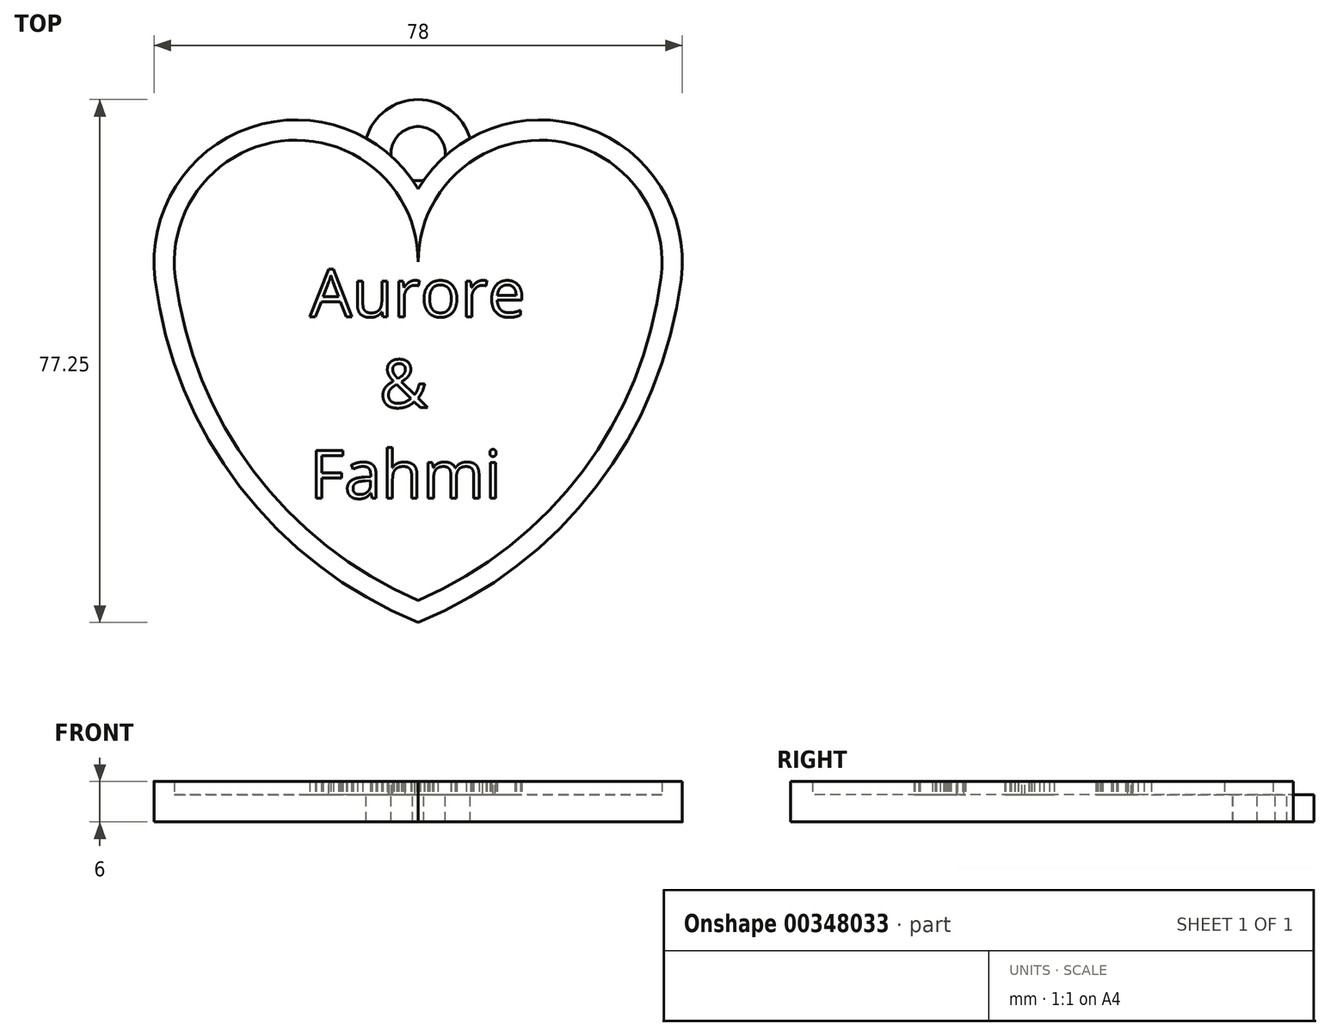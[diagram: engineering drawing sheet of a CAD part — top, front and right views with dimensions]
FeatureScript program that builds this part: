
annotation { "Feature Type Name" : "Feature", "Feature Type Description" : "" }
export const myFeature = defineFeature(function(context is Context, id is Id, definition is map)
    precondition{}
    {
        {
            var Q0;
            Q0=qCreatedBy(makeId("Top.planeOp"),FACE);
            var sketch = newSketch(context, id + "F0", { "sketchPlane" : qUnion([Q0])});
            skArc(sketch, "E0", {"start": v(35.87, -2.2) * mm, "mid": v(19.1, 17.97) * mm, "end": v(0, 0) * mm});
            skLineSegment(sketch, "E1", {"start": v(76.7, -35.15) * mm, "end": v(76.7, -35.15) * mm});
            skArc(sketch, "E2", {"start": v(0, 0) * mm, "mid": v(-19.1, 17.97) * mm, "end": v(-35.87, -2.2) * mm});
            skArc(sketch, "E3", {"start": v(0, -50) * mm, "mid": v(24.3, -30.88) * mm, "end": v(35.87, -2.2) * mm});
            skArc(sketch, "E4.MirrorCS", {"start": v(0, -50) * mm, "mid": v(-24.3, -30.88) * mm, "end": v(-35.87, -2.2) * mm});
            skArc(sketch, "E5", {"start": v(7.93, 14.92) * mm, "mid": v(0, 24) * mm, "end": v(-7.93, 14.92) * mm});
            skText(sketch, "E6", { "text": "Aurore\n    &\nFahmi", "fontName": "OpenSans-Regular.ttf"});
            skArc(sketch, "E7.0", {"start": v(0, -53.25) * mm, "mid": v(26.32, -33.2) * mm, "end": v(38.84, -2.56) * mm});
            skArc(sketch, "E7.1", {"start": v(0, -53.25) * mm, "mid": v(-26.32, -33.2) * mm, "end": v(-38.84, -2.56) * mm});
            skArc(sketch, "E7.2", {"start": v(0, 10.82) * mm, "mid": v(-24.84, 19.86) * mm, "end": v(-38.84, -2.56) * mm});
            skArc(sketch, "E7.3", {"start": v(38.84, -2.56) * mm, "mid": v(24.84, 19.86) * mm, "end": v(0, 10.82) * mm});
            skCircle(sketch, "E8", {"center": v(0, 16) * mm, "radius": 4 * mm});
            const initialGuessF0  = {"E6": [-0.016, -0.0081, 1, 0, 0.0071]};
            skSetInitialGuess(sketch, initialGuessF0);
            skSolve(sketch);
        }
        {
            var Q0;
            Q0 = qSketchRegion(id + "F0", true);
            var Q1;
            {var subQ7=sQuery(id+"F0.wireOp",EDGE,"E3");Q1=makeQuery(id+"F0.imprint","IMPRINT",FACE,{"disambiguationData":[TD([[makeQuery(id+"F0.imprint","IMPRINT",EDGE,{"derivedFrom":subQ7}),1.0]])]});}
            var Q2;
            {var subQ0=sQuery(id+"F0.wireOp",EDGE,"E7.3");var subQ1=sQuery(id+"F0.wireOp",EDGE,"E5");var subQ2=makeQuery(id+"F0.imprint","INTERSECT",VERTEX,{"derivedFrom":[subQ1,subQ0]});Q2=makeQuery(id+"F0.imprint","IMPRINT",FACE,{"disambiguationData":[TD([[makeQuery(id+"F0.imprint","IMPRINT",EDGE,{"disambiguationData":[TD([[subQ2,-1.0]])],"derivedFrom":subQ1}),1.0]])]});}
            var Q3;
            {var subQ0=sQuery(id+"F0.wireOp",EDGE,"E3");Q3=makeQuery(id+"F0.imprint","IMPRINT",FACE,{"disambiguationData":[TD([[makeQuery(id+"F0.imprint","IMPRINT",EDGE,{"derivedFrom":subQ0}),-1.0]])]});}
            var Q4;
            Q4=makeQuery(id+"F0.imprint","IMPRINT",FACE,{"disambiguationData":[TD([[makeQuery(id+"F0.imprint","IMPRINT",EDGE,{"derivedFrom":sQuery(id+"F0.wireOp",EDGE,"E6.sketch_text.stroke-130")}),-1.0]])]});
            var Q5;
            Q5=makeQuery(id+"F0.imprint","IMPRINT",FACE,{"disambiguationData":[TD([[makeQuery(id+"F0.imprint","IMPRINT",EDGE,{"derivedFrom":sQuery(id+"F0.wireOp",EDGE,"E6.sketch_text.stroke-60")}),-1.0]])]});
            var Q6;
            Q6=makeQuery(id+"F0.imprint","IMPRINT",FACE,{"disambiguationData":[TD([[makeQuery(id+"F0.imprint","IMPRINT",EDGE,{"derivedFrom":sQuery(id+"F0.wireOp",EDGE,"E6.sketch_text.stroke-167")}),-1.0]])]});
            var Q7;
            Q7=makeQuery(id+"F0.imprint","IMPRINT",FACE,{"disambiguationData":[TD([[makeQuery(id+"F0.imprint","IMPRINT",EDGE,{"derivedFrom":sQuery(id+"F0.wireOp",EDGE,"E6.sketch_text.stroke-185")}),-1.0]])]});
            var Q8;
            Q8=makeQuery(id+"F0.imprint","IMPRINT",FACE,{"disambiguationData":[TD([[makeQuery(id+"F0.imprint","IMPRINT",EDGE,{"derivedFrom":sQuery(id+"F0.wireOp",EDGE,"E6.sketch_text.stroke-213")}),-1.0]])]});
            var Q9;
            {var subQ1=sQuery(id+"F0.wireOp",EDGE,"E2");var subQ5=sQuery(id+"F0.wireOp",EDGE,"E0");var subQ6=makeQuery(id+"F0.imprint","INTERSECT",VERTEX,{"derivedFrom":[subQ5,subQ1]});Q9=makeQuery(id+"F0.imprint","IMPRINT",FACE,{"disambiguationData":[TD([[makeQuery(id+"F0.imprint","IMPRINT",EDGE,{"disambiguationData":[TD([[subQ6,1.0]])],"derivedFrom":subQ5}),-1.0]])]});}
            var Q10;
            Q10=makeQuery(id+"F0.imprint","IMPRINT",FACE,{"disambiguationData":[TD([[makeQuery(id+"F0.imprint","IMPRINT",EDGE,{"derivedFrom":sQuery(id+"F0.wireOp",EDGE,"E6.sketch_text.stroke-140")}),-1.0]])]});
            var Q11;
            Q11=makeQuery(id+"F0.imprint","IMPRINT",FACE,{"disambiguationData":[TD([[makeQuery(id+"F0.imprint","IMPRINT",EDGE,{"derivedFrom":sQuery(id+"F0.wireOp",EDGE,"E6.sketch_text.stroke-13")}),-1.0]])]});
            var Q12;
            Q12=makeQuery(id+"F0.imprint","IMPRINT",FACE,{"disambiguationData":[TD([[makeQuery(id+"F0.imprint","IMPRINT",EDGE,{"derivedFrom":sQuery(id+"F0.wireOp",EDGE,"E6.sketch_text.stroke-30")}),-1.0]])]});
            var Q13;
            Q13=makeQuery(id+"F0.imprint","IMPRINT",FACE,{"disambiguationData":[TD([[makeQuery(id+"F0.imprint","IMPRINT",EDGE,{"derivedFrom":sQuery(id+"F0.wireOp",EDGE,"E6.sketch_text.stroke-92")}),-1.0]])]});
            var Q14;
            {var subQ0=sQuery(id+"F0.wireOp",EDGE,"E8");var subQ1=sQuery(id+"F0.wireOp",EDGE,"E7.2");var subQ2=makeQuery(id+"F0.imprint","INTERSECT",VERTEX,{"disambiguationData":[OD(0.0)],"derivedFrom":[subQ1,subQ0]});Q14=makeQuery(id+"F0.imprint","IMPRINT",FACE,{"disambiguationData":[TD([[makeQuery(id+"F0.imprint","IMPRINT",EDGE,{"disambiguationData":[TD([[subQ2,-1.0]])],"derivedFrom":subQ1}),1.0]])]});}
            var Q15;
            {var subQ0=sQuery(id+"F0.wireOp",EDGE,"E8");var subQ1=sQuery(id+"F0.wireOp",EDGE,"E7.3");var subQ2=makeQuery(id+"F0.imprint","INTERSECT",VERTEX,{"disambiguationData":[OD(0.0)],"derivedFrom":[subQ1,subQ0]});Q15=makeQuery(id+"F0.imprint","IMPRINT",FACE,{"disambiguationData":[TD([[makeQuery(id+"F0.imprint","IMPRINT",EDGE,{"disambiguationData":[TD([[subQ2,-1.0]])],"derivedFrom":subQ1}),1.0]])]});}
            var Q16;
            Q16=makeQuery(id+"F0.imprint","IMPRINT",FACE,{"disambiguationData":[TD([[makeQuery(id+"F0.imprint","IMPRINT",EDGE,{"derivedFrom":sQuery(id+"F0.wireOp",EDGE,"E6.sketch_text.stroke-159")}),1.0]])]});
            var Q17;
            Q17=makeQuery(id+"F0.imprint","IMPRINT",FACE,{"disambiguationData":[TD([[makeQuery(id+"F0.imprint","IMPRINT",EDGE,{"derivedFrom":sQuery(id+"F0.wireOp",EDGE,"E6.sketch_text.stroke-73")}),-1.0]])]});
            var Q18;
            Q18=makeQuery(id+"F0.imprint","IMPRINT",FACE,{"disambiguationData":[TD([[makeQuery(id+"F0.imprint","IMPRINT",EDGE,{"derivedFrom":sQuery(id+"F0.wireOp",EDGE,"E6.sketch_text.stroke-0")}),-1.0]])]});
            var Q19;
            Q19=makeQuery(id+"F0.imprint","IMPRINT",FACE,{"disambiguationData":[TD([[makeQuery(id+"F0.imprint","IMPRINT",EDGE,{"derivedFrom":sQuery(id+"F0.wireOp",EDGE,"E6.sketch_text.stroke-8")}),1.0]])]});
            var Q20;
            Q20=makeQuery(id+"F0.imprint","IMPRINT",FACE,{"disambiguationData":[TD([[makeQuery(id+"F0.imprint","IMPRINT",EDGE,{"derivedFrom":sQuery(id+"F0.wireOp",EDGE,"E6.sketch_text.stroke-100")}),1.0]])]});
            var Q21;
            {var subQ0=sQuery(id+"F0.wireOp",EDGE,"E7.3");var subQ1=sQuery(id+"F0.wireOp",EDGE,"E7.2");var subQ2=makeQuery(id+"F0.imprint","INTERSECT",VERTEX,{"derivedFrom":[subQ1,subQ0]});Q21=makeQuery(id+"F0.imprint","IMPRINT",FACE,{"disambiguationData":[TD([[makeQuery(id+"F0.imprint","IMPRINT",EDGE,{"disambiguationData":[TD([[subQ2,-1.0]])],"derivedFrom":subQ1}),-1.0]])]});}
            var Q22;
            Q22=makeQuery(id+"F0.imprint","IMPRINT",FACE,{"disambiguationData":[TD([[makeQuery(id+"F0.imprint","IMPRINT",EDGE,{"derivedFrom":sQuery(id+"F0.wireOp",EDGE,"E6.sketch_text.stroke-43")}),-1.0]])]});
            var Q23;
            Q23=makeQuery(id+"F0.imprint","IMPRINT",FACE,{"disambiguationData":[TD([[makeQuery(id+"F0.imprint","IMPRINT",EDGE,{"derivedFrom":sQuery(id+"F0.wireOp",EDGE,"E6.sketch_text.stroke-52")}),1.0]])]});
            var Q24;
            Q24=makeQuery(id+"F0.imprint","IMPRINT",FACE,{"disambiguationData":[TD([[makeQuery(id+"F0.imprint","IMPRINT",EDGE,{"derivedFrom":sQuery(id+"F0.wireOp",EDGE,"E6.sketch_text.stroke-92")}),1.0]])]});
            var Q25;
            Q25=makeQuery(id+"F0.imprint","IMPRINT",FACE,{"disambiguationData":[TD([[makeQuery(id+"F0.imprint","IMPRINT",EDGE,{"derivedFrom":sQuery(id+"F0.wireOp",EDGE,"E6.sketch_text.stroke-87")}),1.0]])]});
            var Q26;
            Q26=makeQuery(id+"F0.imprint","IMPRINT",FACE,{"disambiguationData":[TD([[makeQuery(id+"F0.imprint","IMPRINT",EDGE,{"derivedFrom":sQuery(id+"F0.wireOp",EDGE,"E6.sketch_text.stroke-217")}),-1.0]])]});
            extrude(context, id + "F1", {"entities" : qUnion([Q0, Q1, Q2, Q3, Q4, Q5, Q6, Q7, Q8, Q9, Q10, Q11, Q12, Q13, Q14, Q15, Q16, Q17, Q18, Q19, Q20, Q21, Q22, Q23, Q24, Q25, Q26]), "oppositeDirection" : true, "depth" : 4 * mm});
        }
        {
            var Q0;
            Q0=makeQuery(id+"F0.imprint","IMPRINT",FACE,{"disambiguationData":[TD([[makeQuery(id+"F0.imprint","IMPRINT",EDGE,{"derivedFrom":sQuery(id+"F0.wireOp",EDGE,"E6.sketch_text.stroke-0")}),-1.0]])]});
            var Q1;
            Q1=makeQuery(id+"F0.imprint","IMPRINT",FACE,{"disambiguationData":[TD([[makeQuery(id+"F0.imprint","IMPRINT",EDGE,{"derivedFrom":sQuery(id+"F0.wireOp",EDGE,"E6.sketch_text.stroke-13")}),-1.0]])]});
            var Q2;
            Q2=makeQuery(id+"F0.imprint","IMPRINT",FACE,{"disambiguationData":[TD([[makeQuery(id+"F0.imprint","IMPRINT",EDGE,{"derivedFrom":sQuery(id+"F0.wireOp",EDGE,"E6.sketch_text.stroke-30")}),-1.0]])]});
            var Q3;
            Q3=makeQuery(id+"F0.imprint","IMPRINT",FACE,{"disambiguationData":[TD([[makeQuery(id+"F0.imprint","IMPRINT",EDGE,{"derivedFrom":sQuery(id+"F0.wireOp",EDGE,"E6.sketch_text.stroke-43")}),-1.0]])]});
            var Q4;
            Q4=makeQuery(id+"F0.imprint","IMPRINT",FACE,{"disambiguationData":[TD([[makeQuery(id+"F0.imprint","IMPRINT",EDGE,{"derivedFrom":sQuery(id+"F0.wireOp",EDGE,"E6.sketch_text.stroke-60")}),-1.0]])]});
            var Q5;
            Q5=makeQuery(id+"F0.imprint","IMPRINT",FACE,{"disambiguationData":[TD([[makeQuery(id+"F0.imprint","IMPRINT",EDGE,{"derivedFrom":sQuery(id+"F0.wireOp",EDGE,"E6.sketch_text.stroke-73")}),-1.0]])]});
            var Q6;
            Q6=makeQuery(id+"F0.imprint","IMPRINT",FACE,{"disambiguationData":[TD([[makeQuery(id+"F0.imprint","IMPRINT",EDGE,{"derivedFrom":sQuery(id+"F0.wireOp",EDGE,"E6.sketch_text.stroke-92")}),-1.0]])]});
            var Q7;
            Q7=makeQuery(id+"F0.imprint","IMPRINT",FACE,{"disambiguationData":[TD([[makeQuery(id+"F0.imprint","IMPRINT",EDGE,{"derivedFrom":sQuery(id+"F0.wireOp",EDGE,"E6.sketch_text.stroke-130")}),-1.0]])]});
            var Q8;
            Q8=makeQuery(id+"F0.imprint","IMPRINT",FACE,{"disambiguationData":[TD([[makeQuery(id+"F0.imprint","IMPRINT",EDGE,{"derivedFrom":sQuery(id+"F0.wireOp",EDGE,"E6.sketch_text.stroke-140")}),-1.0]])]});
            var Q9;
            Q9=makeQuery(id+"F0.imprint","IMPRINT",FACE,{"disambiguationData":[TD([[makeQuery(id+"F0.imprint","IMPRINT",EDGE,{"derivedFrom":sQuery(id+"F0.wireOp",EDGE,"E6.sketch_text.stroke-167")}),-1.0]])]});
            var Q10;
            Q10=makeQuery(id+"F0.imprint","IMPRINT",FACE,{"disambiguationData":[TD([[makeQuery(id+"F0.imprint","IMPRINT",EDGE,{"derivedFrom":sQuery(id+"F0.wireOp",EDGE,"E6.sketch_text.stroke-185")}),-1.0]])]});
            var Q11;
            Q11=makeQuery(id+"F0.imprint","IMPRINT",FACE,{"disambiguationData":[TD([[makeQuery(id+"F0.imprint","IMPRINT",EDGE,{"derivedFrom":sQuery(id+"F0.wireOp",EDGE,"E6.sketch_text.stroke-213")}),-1.0]])]});
            var Q12;
            Q12=makeQuery(id+"F0.imprint","IMPRINT",FACE,{"disambiguationData":[TD([[makeQuery(id+"F0.imprint","IMPRINT",EDGE,{"derivedFrom":sQuery(id+"F0.wireOp",EDGE,"E6.sketch_text.stroke-217")}),-1.0]])]});
            var Q13;
            {var subQ1=sQuery(id+"F0.wireOp",EDGE,"E2");var subQ5=sQuery(id+"F0.wireOp",EDGE,"E0");var subQ6=makeQuery(id+"F0.imprint","INTERSECT",VERTEX,{"derivedFrom":[subQ5,subQ1]});Q13=makeQuery(id+"F0.imprint","IMPRINT",FACE,{"disambiguationData":[TD([[makeQuery(id+"F0.imprint","IMPRINT",EDGE,{"disambiguationData":[TD([[subQ6,1.0]])],"derivedFrom":subQ5}),-1.0]])]});}
            var Q14;
            {var subQ0=sQuery(id+"F0.wireOp",EDGE,"E3");Q14=makeQuery(id+"F0.imprint","IMPRINT",FACE,{"disambiguationData":[TD([[makeQuery(id+"F0.imprint","IMPRINT",EDGE,{"derivedFrom":subQ0}),-1.0]])]});}
            var Q15;
            {var subQ0=sQuery(id+"F0.wireOp",EDGE,"E8");var subQ1=sQuery(id+"F0.wireOp",EDGE,"E7.2");var subQ2=makeQuery(id+"F0.imprint","INTERSECT",VERTEX,{"disambiguationData":[OD(0.0)],"derivedFrom":[subQ1,subQ0]});Q15=makeQuery(id+"F0.imprint","IMPRINT",FACE,{"disambiguationData":[TD([[makeQuery(id+"F0.imprint","IMPRINT",EDGE,{"disambiguationData":[TD([[subQ2,-1.0]])],"derivedFrom":subQ1}),1.0]])]});}
            var Q16;
            {var subQ0=sQuery(id+"F0.wireOp",EDGE,"E8");var subQ1=sQuery(id+"F0.wireOp",EDGE,"E7.3");var subQ2=makeQuery(id+"F0.imprint","INTERSECT",VERTEX,{"disambiguationData":[OD(0.0)],"derivedFrom":[subQ1,subQ0]});Q16=makeQuery(id+"F0.imprint","IMPRINT",FACE,{"disambiguationData":[TD([[makeQuery(id+"F0.imprint","IMPRINT",EDGE,{"disambiguationData":[TD([[subQ2,-1.0]])],"derivedFrom":subQ1}),1.0]])]});}
            extrude(context, id + "F2", {"entities" : qUnion([Q0, Q1, Q2, Q3, Q4, Q5, Q6, Q7, Q8, Q9, Q10, Q11, Q12, Q13, Q14, Q15, Q16]), "operationType" : NewBodyOperationType.ADD, "depth" : 2 * mm});
        }
    });
